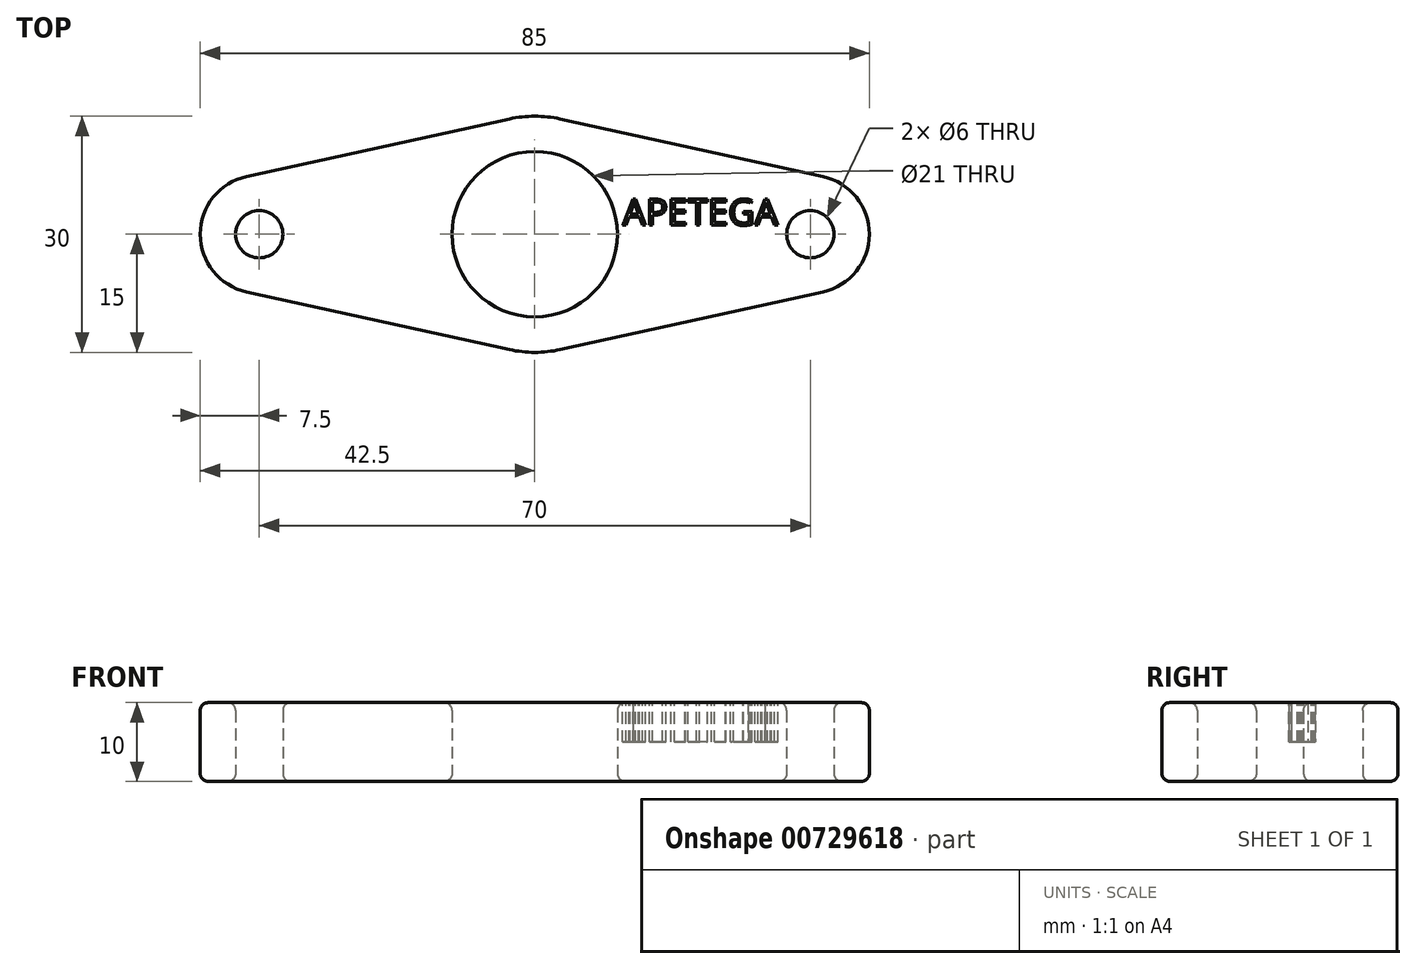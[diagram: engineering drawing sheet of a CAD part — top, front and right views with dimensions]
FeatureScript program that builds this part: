
annotation { "Feature Type Name" : "Feature", "Feature Type Description" : "" }
export const myFeature = defineFeature(function(context is Context, id is Id, definition is map)
    precondition{}
    {
        {
            var Q0;
            Q0=qCreatedBy(makeId("Top.planeOp"),FACE);
            var sketch = newSketch(context, id + "F0", { "sketchPlane" : qUnion([Q0])});
            skCircle(sketch, "E0", {"center": v(0, 0) * mm, "radius": 10.5 * mm});
            skArc(sketch, "E1", {"start": v(-3.21, -14.65) * mm, "mid": v(0, -15) * mm, "end": v(3.21, -14.65) * mm});
            skLineSegment(sketch, "E2", {"start": v(0, 0) * mm, "end": v(35, 0) * mm, "construction": true});
            skLineSegment(sketch, "E3", {"start": v(0, 0) * mm, "end": v(-35, 0) * mm, "construction": true});
            skCircle(sketch, "E4", {"center": v(35, 0) * mm, "radius": 3 * mm});
            skCircle(sketch, "E5", {"center": v(-35, 0) * mm, "radius": 3 * mm});
            skArc(sketch, "E6", {"start": v(36.6, -7.33) * mm, "mid": v(42.5, 0) * mm, "end": v(36.6, 7.33) * mm});
            skArc(sketch, "E7", {"start": v(-36.6, 7.33) * mm, "mid": v(-42.5, 0) * mm, "end": v(-36.6, -7.33) * mm});
            skLineSegment(sketch, "E8", {"start": v(3.21, 14.65) * mm, "end": v(36.6, 7.33) * mm});
            skPoint(sketch, "E9.orphan", {"position": v(70, 0) * mm});
            skLineSegment(sketch, "E10", {"start": v(3.21, -14.65) * mm, "end": v(36.6, -7.33) * mm});
            skLineSegment(sketch, "E11", {"start": v(-36.6, -7.33) * mm, "end": v(-3.21, -14.65) * mm});
            skLineSegment(sketch, "E12", {"start": v(-36.6, 7.33) * mm, "end": v(-3.21, 14.65) * mm});
            skArc(sketch, "E13.trimOffspring", {"start": v(3.21, 14.65) * mm, "mid": v(0, 15) * mm, "end": v(-3.21, 14.65) * mm});
            skSolve(sketch);
        }
        {
            var Q0;
            Q0 = qSketchRegion(id + "F0", true);
            extrude(context, id + "F1", {"entities" : qUnion([Q0]), "depth" : 10 * mm, "offsetDistance" : 25 * mm});
        }
        {
            var Q0;
            Q0=makeQuery(id+"F1.opExtrude","CAP_FACE",FACE,{"disambiguationData":[OSD([sQuery(id+"F0.wireOp",EDGE,"E0"),sQuery(id+"F0.wireOp",EDGE,"E1"),sQuery(id+"F0.wireOp",EDGE,"E4"),sQuery(id+"F0.wireOp",EDGE,"E5"),sQuery(id+"F0.wireOp",EDGE,"E6"),sQuery(id+"F0.wireOp",EDGE,"E7"),sQuery(id+"F0.wireOp",EDGE,"E8"),sQuery(id+"F0.wireOp",EDGE,"E10"),sQuery(id+"F0.wireOp",EDGE,"E11"),sQuery(id+"F0.wireOp",EDGE,"E12"),sQuery(id+"F0.wireOp",EDGE,"E13.trimOffspring")])],"isStart":false});
            fillet(context, id + "F2", {"entities" : qUnion([Q0]), "radius" : 1 * mm, "tangentPropagation" : true, "allowEdgeOverflow" : false});
        }
        {
            var Q0;
            Q0=makeQuery(id+"F1.opExtrude","CAP_FACE",FACE,{"disambiguationData":[OSD([sQuery(id+"F0.wireOp",EDGE,"E0"),sQuery(id+"F0.wireOp",EDGE,"E1"),sQuery(id+"F0.wireOp",EDGE,"E4"),sQuery(id+"F0.wireOp",EDGE,"E5"),sQuery(id+"F0.wireOp",EDGE,"E6"),sQuery(id+"F0.wireOp",EDGE,"E7"),sQuery(id+"F0.wireOp",EDGE,"E8"),sQuery(id+"F0.wireOp",EDGE,"E10"),sQuery(id+"F0.wireOp",EDGE,"E11"),sQuery(id+"F0.wireOp",EDGE,"E12"),sQuery(id+"F0.wireOp",EDGE,"E13.trimOffspring")])],"isStart":true});
            fillet(context, id + "F3", {"entities" : qUnion([Q0]), "radius" : 1 * mm, "tangentPropagation" : true, "allowEdgeOverflow" : false});
        }
        {
            var Q0;
            Q0=makeQuery(id+"F1.opExtrude","CAP_FACE",FACE,{"disambiguationData":[OSD([sQuery(id+"F0.wireOp",EDGE,"E0"),sQuery(id+"F0.wireOp",EDGE,"E1"),sQuery(id+"F0.wireOp",EDGE,"E4"),sQuery(id+"F0.wireOp",EDGE,"E5"),sQuery(id+"F0.wireOp",EDGE,"E6"),sQuery(id+"F0.wireOp",EDGE,"E7"),sQuery(id+"F0.wireOp",EDGE,"E8"),sQuery(id+"F0.wireOp",EDGE,"E10"),sQuery(id+"F0.wireOp",EDGE,"E11"),sQuery(id+"F0.wireOp",EDGE,"E12"),sQuery(id+"F0.wireOp",EDGE,"E13.trimOffspring")])],"isStart":false});
            var sketch = newSketch(context, id + "F4", { "sketchPlane" : qUnion([Q0])});
            skText(sketch, "E14", { "text": "APETEGA\n", "fontName": "OpenSans-Regular.ttf"});
            const initialGuessF4  = {"E14": [0.01117, 0.00115, 1, 0, 0.00333]};
            skSetInitialGuess(sketch, initialGuessF4);
            skSolve(sketch);
        }
        {
            var Q0;
            Q0 = qSketchRegion(id + "F4", true);
            extrude(context, id + "F5", {"entities" : qUnion([Q0]), "operationType" : NewBodyOperationType.REMOVE, "oppositeDirection" : true, "depth" : 5 * mm, "offsetDistance" : 25 * mm});
        }
    });
